# Revit family: Bi_Level-Drinking_Fountain-Bottle_Filler-Murdock_Mfg-H2O-to-Go-A172.8-UG-BF12_Series
name_source: partatom
category: Plumbing Fixtures
units: mm (PartAtom-declared; Revit-internal decimal feet)

## family parameters
Cut with Voids When Loaded = Yes
Host = Face
OmniClass Number = 23.65.70.14.11
OmniClass Title = Drinking Fountains/Coolers
Part Type = Normal
Room Calculation Point = No
Round Connector Dimension = Use Diameter
Shared = Yes

## types (4) — shared parameters
-220V 220 Volt / 50 Hz or 60Hz Compressor = No
-BF11 Bottle Filler with Pushbutton Operation = No
-BF12 Bottle Filler with Sensor Operation = Yes
-BF12-BAT Bottle Filler with Battery Operated Sensor Operation = No
-BF12-BCD Bottle Filler with Sensor Operation with = No
-LOGO Customer Specified Logo / Graphics = No
-SK5 Skirt Kit for upper unit = No
-WF3EZ 3000-Gallon EZ Door PFAS Filter NSF/PFAS/Lead Bacteria/Chlorine/Microplastics = No
115VAC Plug-In Transformer = No
ADA Compliant = Yes
Activation = Push Button or Sensor Operated
Assembly Code = D2010820
Bottle Filler Type = Bottle_Filler-Murdock-H2O-To-Go-BFI1-BF12_Series : BF12
Bubbler1 Height A.F.F. = 33"
CW Connection = Yes
CWFU = 1.5
Cold Water Connection Diameter = 3/8"
Cold Water Connection Height = 19 3/8"
Cold Water Connection Width = 2"
Compliance Certifications = ANSI/ASHRAE 18, IAPMO tested to NSF/ANSI 61, Section 9, UL Listed (US and Canada), cUPC, CE complaint for 220 V electrical, Lead-Free Federal Law 111-380
Default Elevation = 0"
Description = Wall-Mounted, Bi-Level, Push Button Drinking Fountain with H2O-to-Go!® Touchless Water Bottle Filling Station - In-Unit Refrigeration (8GPH), ADA, Stainless Steel
Finish- Bottle Filler Housing = Stainless Steel-Murdock-Satin
Finish- Others = Plastic-Murdock-Black
Finish- Push Button = Brass-Murdock-Chrome Plated
Flow Rate = 1.00 GPM
HW Connection = No
Height = 47 5/8"
Height- Bottle Filler Sensor = 40 7/8"
Installation Type = Wall Mounted
Laminar (LAM) = Yes
Length = 18 1/2"
Manufacturer = Murdock Manufacturing
Product Documentation Link = https://www.murdockmfg.com
Product Page URL = https://www.murdockmfg.com
Sensor Operated = No
URL = https://www.murdockmfg.com
Vent Connection = No
Voltage Nominal = 0 V
WFU = 2
Waste Connection = Yes
Waste Connection Diameter = 1 1/4"
Waste Connection Height = 22 1/4"
Water Pressure = 20-105 PSIG
Width = 37 1/8"
cUPC Compliant = Yes
zero-valued in all types: HWFU

## per-type parameters (varying)
| type | Bubbler2 Height A.F.F. | Finish | Finish- Bubbler | Flexible Bubbler  A172408F-UG Satin Stainless Finish | Flexible Bubbler A172108F-UG Gray Finish Cooler | Material | Stainless Steel Bubbler A172108S-UG Gray Finish Cooler | Stainless Steel Bubbler A172408S-UG Satin Stainless Finish |
| A172408S-UG-BF12 | 39" | Stainless Steel-Murdock-Satin | Stainless Steel-Murdock-Satin | No | No | Stainless Steel-Murdock-Satin | No | Yes |
| A172408F-UG-BF12 | 0" | Stainless Steel-Murdock-Satin | Stainless Steel-Murdock-Satin-Flexible | Yes | No | Stainless Steel-Murdock-Satin | No | No |
| A172108F-UG-BF12 | 0" | Stainless Steel-Murdock-Textured Grey Finish | Stainless Steel-Murdock-Satin-Flexible | No | Yes | Stainless Steel-Murdock-Textured Grey Finish | No | No |
| A172108S-UG-BF12 | 39" | Stainless Steel-Murdock-Textured Grey Finish | Stainless Steel-Murdock-Satin | No | No | Stainless Steel-Murdock-Textured Grey Finish | Yes | No |

note: column(s) folded — value = type name in every type: Model

## geometry (parser evidence)
native form markers: Sweep x5
no freeform markers — native parametric forms only
